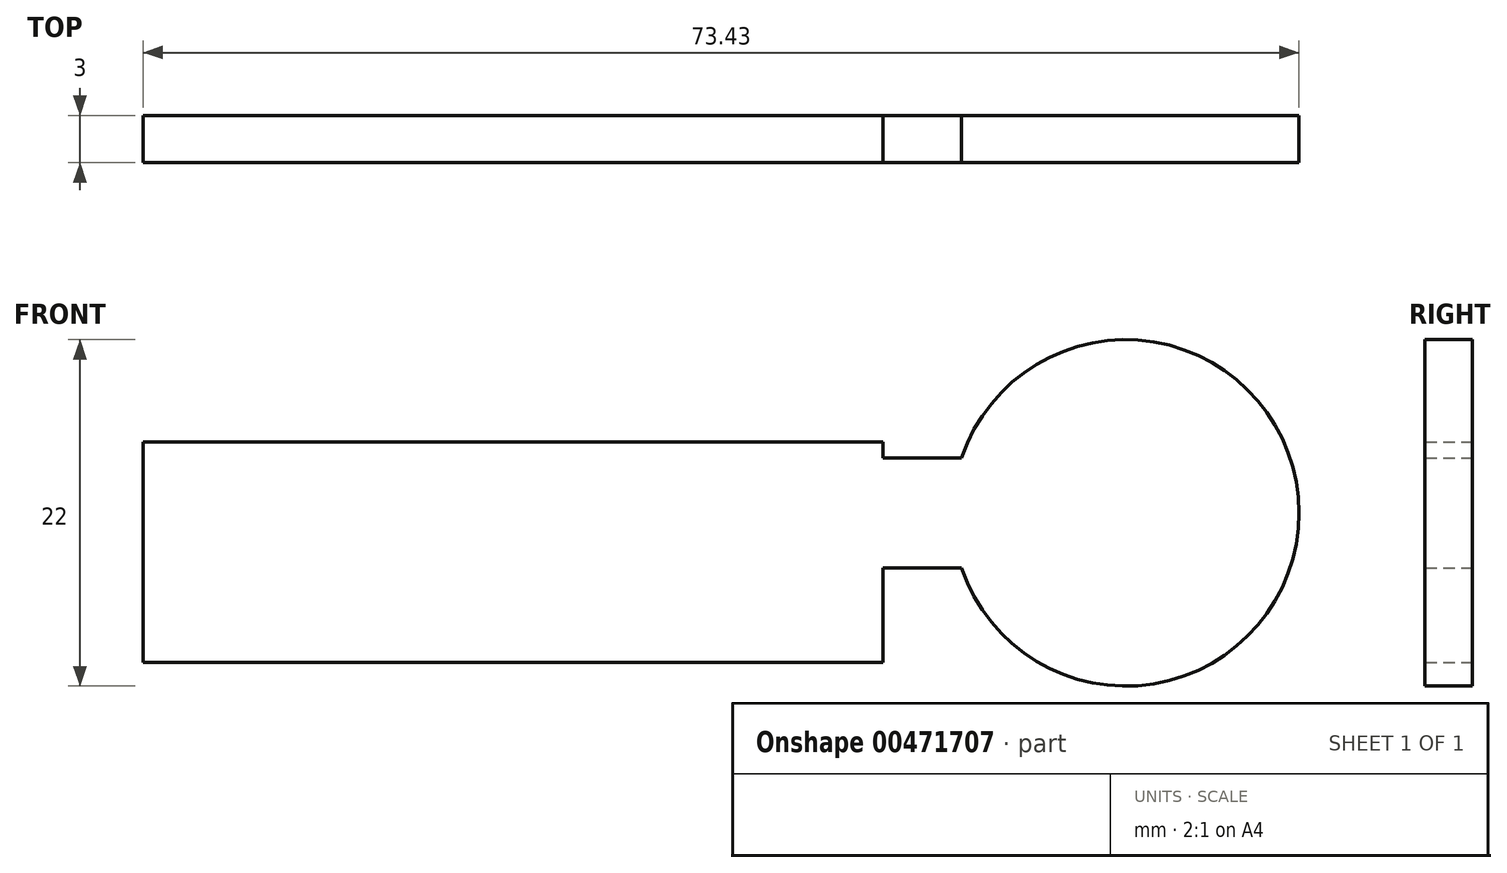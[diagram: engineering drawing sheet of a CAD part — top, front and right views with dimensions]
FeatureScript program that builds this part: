
annotation { "Feature Type Name" : "Feature", "Feature Type Description" : "" }
export const myFeature = defineFeature(function(context is Context, id is Id, definition is map)
    precondition{}
    {
        {
            var Q0;
            Q0=qCreatedBy(makeId("Front.planeOp"),FACE);
            var sketch = newSketch(context, id + "F0", { "sketchPlane" : qUnion([Q0])});
            skLineSegment(sketch, "E0.bottom", {"start": v(0, 0) * mm, "end": v(40, 0) * mm});
            skLineSegment(sketch, "E0.top", {"start": v(0, 7) * mm, "end": v(40, 7) * mm});
            skLineSegment(sketch, "E0.left", {"start": v(0, 0) * mm, "end": v(0, 7) * mm});
            skLineSegment(sketch, "E0.right", {"start": v(40, 0) * mm, "end": v(40, 7) * mm});
            skArc(sketch, "E1", {"start": v(40, 0) * mm, "mid": v(61.43, 3.5) * mm, "end": v(40, 7) * mm});
            skLineSegment(sketch, "E2", {"start": v(0, 7) * mm, "end": v(-10, 2.5) * mm});
            skLineSegment(sketch, "E3", {"start": v(-10, 2.5) * mm, "end": v(-10, -2) * mm});
            skLineSegment(sketch, "E4", {"start": v(-10, -2) * mm, "end": v(-2, -2) * mm});
            skLineSegment(sketch, "E5", {"start": v(-2, -2) * mm, "end": v(8, 4) * mm});
            skLineSegment(sketch, "E6", {"start": v(8, 4) * mm, "end": v(13, 4) * mm});
            skLineSegment(sketch, "E7", {"start": v(13, 4) * mm, "end": v(15, -2.5) * mm});
            skLineSegment(sketch, "E8", {"start": v(15, -2.5) * mm, "end": v(11.75, -3.5) * mm});
            skLineSegment(sketch, "E9", {"start": v(11.75, -3.5) * mm, "end": v(15, -5) * mm});
            skLineSegment(sketch, "E10", {"start": v(15, -5) * mm, "end": v(32, 0) * mm});
            skCircle(sketch, "E11", {"center": v(57.43, 3.5) * mm, "radius": 3 * mm});
            skLineSegment(sketch, "E12.bottom", {"start": v(-12, 8) * mm, "end": v(35, 8) * mm});
            skLineSegment(sketch, "E12.top", {"start": v(-12, -6) * mm, "end": v(35, -6) * mm});
            skLineSegment(sketch, "E12.left", {"start": v(-12, 8) * mm, "end": v(-12, -6) * mm});
            skLineSegment(sketch, "E12.right", {"start": v(35, 8) * mm, "end": v(35, -6) * mm});
            skSolve(sketch);
        }
        {
            var Q0;
            {var subQ0=sQuery(id+"F0.wireOp",EDGE,"E0.left");Q0=makeQuery(id+"F0.imprint","IMPRINT",FACE,{"disambiguationData":[TD([[makeQuery(id+"F0.imprint","IMPRINT",EDGE,{"derivedFrom":subQ0}),1.0]])]});}
            var Q1;
            {var subQ9=sQuery(id+"F0.wireOp",EDGE,"E0.left");Q1=makeQuery(id+"F0.imprint","IMPRINT",FACE,{"disambiguationData":[TD([[makeQuery(id+"F0.imprint","IMPRINT",EDGE,{"derivedFrom":subQ9}),-1.0]])]});}
            var Q2;
            {var subQ4=sQuery(id+"F0.wireOp",EDGE,"E8");Q2=makeQuery(id+"F0.imprint","IMPRINT",FACE,{"disambiguationData":[TD([[makeQuery(id+"F0.imprint","IMPRINT",EDGE,{"derivedFrom":subQ4}),1.0]])]});}
            var Q3;
            {var subQ3=sQuery(id+"F0.wireOp",EDGE,"7VBHRefb-ZezH-LXmD-XGCx-hcoTWlabLQlG");Q3=makeQuery(id+"F0.imprint","IMPRINT",FACE,{"disambiguationData":[TD([[makeQuery(id+"F0.imprint","IMPRINT",EDGE,{"derivedFrom":subQ3}),-1.0]])]});}
            var Q4;
            {var subQ3=sQuery(id+"F0.wireOp",EDGE,"lKG2LDTI-TQmS-NmJ1-liUh-qlYl0mUGQLIu");Q4=makeQuery(id+"F0.imprint","IMPRINT",FACE,{"disambiguationData":[TD([[makeQuery(id+"F0.imprint","IMPRINT",EDGE,{"derivedFrom":subQ3}),-1.0]])]});}
            var Q5;
            {var subQ0=sQuery(id+"F0.wireOp",EDGE,"E0.right");Q5=makeQuery(id+"F0.imprint","IMPRINT",FACE,{"disambiguationData":[TD([[makeQuery(id+"F0.imprint","IMPRINT",EDGE,{"derivedFrom":subQ0}),1.0]])]});}
            var Q6;
            {var subQ0=sQuery(id+"F0.wireOp",EDGE,"E0.right");Q6=makeQuery(id+"F0.imprint","IMPRINT",FACE,{"disambiguationData":[TD([[makeQuery(id+"F0.imprint","IMPRINT",EDGE,{"derivedFrom":subQ0}),-1.0]])]});}
            var Q7;
            {var subQ5=sQuery(id+"F0.wireOp",EDGE,"E6");Q7=makeQuery(id+"F0.imprint","IMPRINT",FACE,{"disambiguationData":[TD([[makeQuery(id+"F0.imprint","IMPRINT",EDGE,{"derivedFrom":subQ5}),-1.0]])]});}
            var Q8;
            {var subQ10=sQuery(id+"F0.wireOp",EDGE,"E2");Q8=makeQuery(id+"F0.imprint","IMPRINT",FACE,{"disambiguationData":[TD([[makeQuery(id+"F0.imprint","IMPRINT",EDGE,{"derivedFrom":subQ10}),-1.0]])]});}
            var Q9;
            Q9=makeQuery(id+"F0.imprint","IMPRINT",FACE,{"disambiguationData":[TD([[makeQuery(id+"F0.imprint","IMPRINT",EDGE,{"derivedFrom":sQuery(id+"F0.wireOp",EDGE,"E11")}),1.0]])]});
            extrude(context, id + "F1", {"entities" : qUnion([Q0, Q1, Q2, Q3, Q4, Q5, Q6, Q7, Q8, Q9]), "depth" : 3 * mm});
        }
    });
